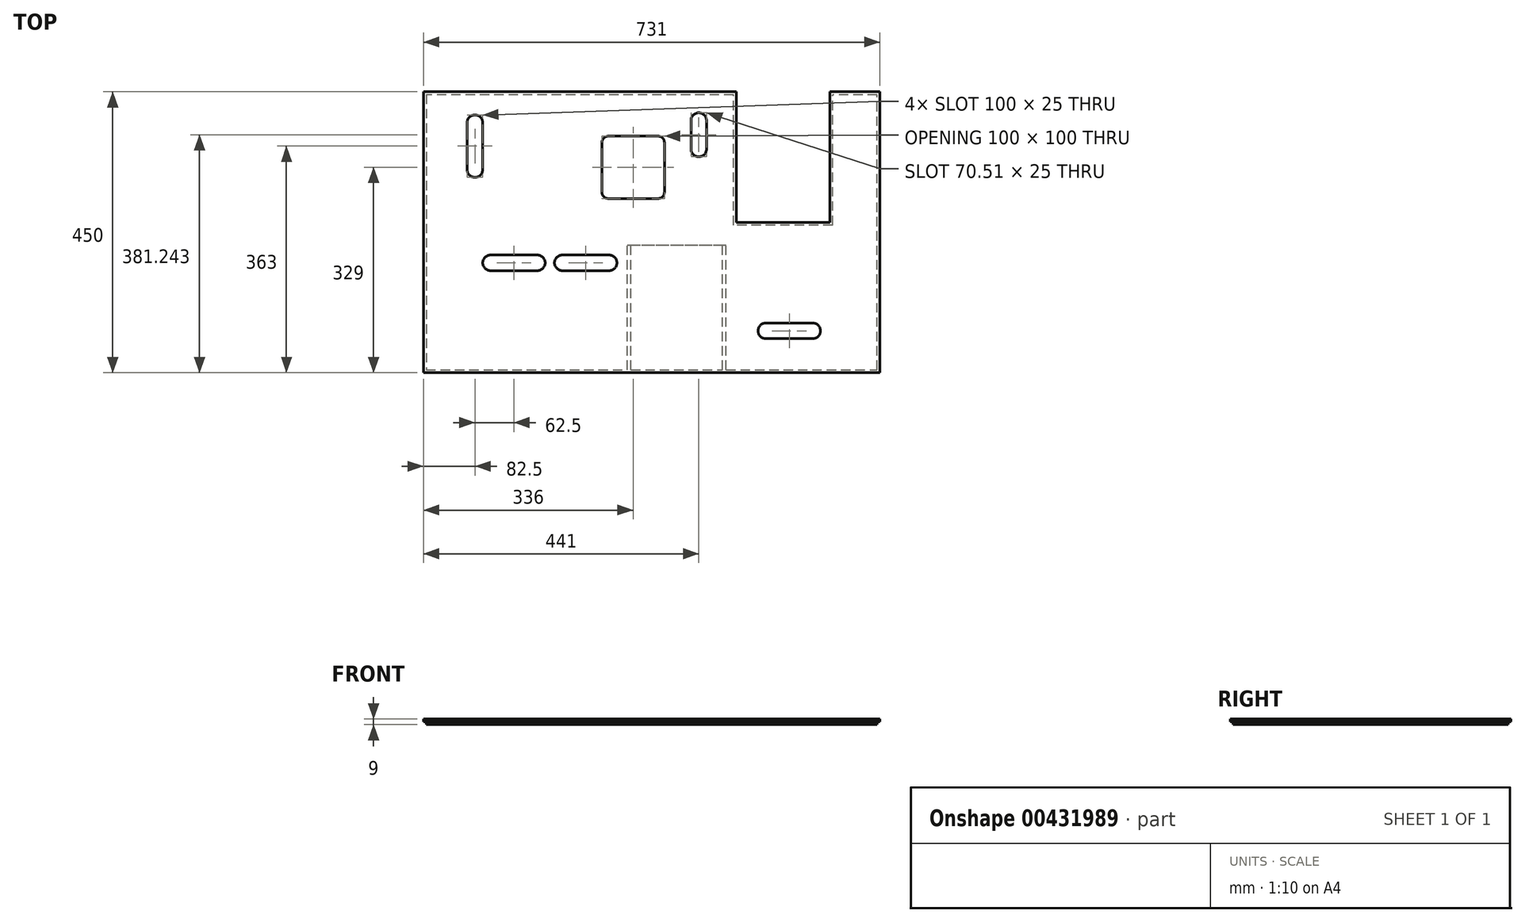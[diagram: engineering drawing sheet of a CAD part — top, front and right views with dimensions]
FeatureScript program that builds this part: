
annotation { "Feature Type Name" : "Feature", "Feature Type Description" : "" }
export const myFeature = defineFeature(function(context is Context, id is Id, definition is map)
    precondition{}
    {
        {
            var Q0;
            Q0=qCreatedBy(makeId("Top.planeOp"),FACE);
            var sketch = newSketch(context, id + "F0", { "sketchPlane" : qUnion([Q0])});
            skLineSegment(sketch, "E0.bottom", {"start": v(-365.5, 225) * mm, "end": v(365.5, 225) * mm});
            skLineSegment(sketch, "E0.top", {"start": v(-365.5, -225) * mm, "end": v(365.5, -225) * mm});
            skLineSegment(sketch, "E0.left", {"start": v(-365.5, 225) * mm, "end": v(-365.5, -225) * mm});
            skLineSegment(sketch, "E0.right", {"start": v(365.5, 225) * mm, "end": v(365.5, -225) * mm});
            skPoint(sketch, "E0.middle", {"position": v(0, 0) * mm});
            skSolve(sketch);
        }
        {
            var Q0;
            Q0=makeQuery(id+"F0.imprint","IMPRINT",FACE,{"disambiguationData":[TD([[makeQuery(id+"F0.imprint","IMPRINT",EDGE,{"derivedFrom":sQuery(id+"F0.wireOp",EDGE,"E0.bottom")}),-1.0]])]});
            extrude(context, id + "F1", {"entities" : qUnion([Q0]), "depth" : 9 * mm, "offsetDistance" : 25 * mm});
        }
        {
            var Q0;
            Q0=makeQuery(id+"F1.opExtrude","CAP_FACE",FACE,{"disambiguationData":[OSD([sQuery(id+"F0.wireOp",EDGE,"E0.bottom"),sQuery(id+"F0.wireOp",EDGE,"E0.top"),sQuery(id+"F0.wireOp",EDGE,"E0.left"),sQuery(id+"F0.wireOp",EDGE,"E0.right")])],"isStart":true});
            var sketch = newSketch(context, id + "F2", { "sketchPlane" : qUnion([Q0])});
            skLineSegment(sketch, "E1.0", {"start": v(-361, -220.5) * mm, "end": v(-361, 220.5) * mm});
            skLineSegment(sketch, "E1.1", {"start": v(361, -220.5) * mm, "end": v(-361, -220.5) * mm});
            skLineSegment(sketch, "E1.2", {"start": v(361, 220.5) * mm, "end": v(361, -220.5) * mm});
            skLineSegment(sketch, "E1.3", {"start": v(-361, 220.5) * mm, "end": v(361, 220.5) * mm});
            skLineSegment(sketch, "E2.bottom", {"start": v(-365.5, -225) * mm, "end": v(365.5, -225) * mm});
            skLineSegment(sketch, "E2.top", {"start": v(-365.5, 225) * mm, "end": v(365.5, 225) * mm});
            skLineSegment(sketch, "E2.left", {"start": v(-365.5, 225) * mm, "end": v(-365.5, -225) * mm});
            skLineSegment(sketch, "E2.right", {"start": v(365.5, 225) * mm, "end": v(365.5, -225) * mm});
            skPoint(sketch, "E2.middle", {"position": v(0, 0) * mm});
            skSolve(sketch);
        }
        {
            var Q0;
            Q0=qSketchRegion(id+"F2",true);
            extrude(context, id + "F3", {"entities" : qUnion([Q0]), "operationType" : NewBodyOperationType.REMOVE, "oppositeDirection" : true, "depth" : 4.5 * mm, "offsetDistance" : 25 * mm});
        }
        {
            var Q0;
            Q0=makeQuery(id+"F1.opExtrude","SWEPT_FACE",FACE,{"disambiguationData":[OSD([sQuery(id+"F0.wireOp",EDGE,"E0.bottom")])]});
            var sketch = newSketch(context, id + "F4", { "sketchPlane" : qUnion([Q0])});
            skLineSegment(sketch, "E3.bottom", {"start": v(-285.5, 0) * mm, "end": v(-135.5, 0) * mm});
            skLineSegment(sketch, "E3.top", {"start": v(-285.5, 9) * mm, "end": v(-135.5, 9) * mm});
            skLineSegment(sketch, "E3.left", {"start": v(-285.5, 0) * mm, "end": v(-285.5, 9) * mm});
            skLineSegment(sketch, "E3.right", {"start": v(-135.5, 0) * mm, "end": v(-135.5, 9) * mm});
            skSolve(sketch);
        }
        {
            var Q0;
            Q0=qSketchRegion(id+"F4",true);
            extrude(context, id + "F5", {"entities" : qUnion([Q0]), "operationType" : NewBodyOperationType.REMOVE, "oppositeDirection" : true, "depth" : (174 + 35) * mm, "offsetDistance" : 25 * mm});
        }
        {
            var Q0;
            Q0=makeQuery(id+"F1.opExtrude","CAP_FACE",FACE,{"disambiguationData":[OSD([sQuery(id+"F0.wireOp",EDGE,"E0.bottom"),sQuery(id+"F0.wireOp",EDGE,"E0.top"),sQuery(id+"F0.wireOp",EDGE,"E0.left"),sQuery(id+"F0.wireOp",EDGE,"E0.right")])],"isStart":true});
            var sketch = newSketch(context, id + "F6", { "sketchPlane" : qUnion([Q0])});
            skLineSegment(sketch, "E4.0", {"start": v(290, -16) * mm, "end": v(290, -225) * mm});
            skLineSegment(sketch, "E4.2", {"start": v(131, -16) * mm, "end": v(131, -225) * mm});
            skLineSegment(sketch, "E5", {"start": v(285.5, -225) * mm, "end": v(285.5, -16) * mm});
            skLineSegment(sketch, "E6", {"start": v(285.5, -16) * mm, "end": v(135.5, -16) * mm});
            skLineSegment(sketch, "E7", {"start": v(135.5, -16) * mm, "end": v(135.5, -225) * mm});
            skLineSegment(sketch, "E8", {"start": v(135.5, -225) * mm, "end": v(131, -225) * mm});
            skLineSegment(sketch, "E9", {"start": v(135.5, -16) * mm, "end": v(131, -16) * mm});
            skLineSegment(sketch, "E10", {"start": v(285.5, -16) * mm, "end": v(290, -16) * mm});
            skLineSegment(sketch, "E11", {"start": v(290, -225) * mm, "end": v(285.5, -225) * mm});
            skSolve(sketch);
        }
        {
            var Q0;
            Q0=qSketchRegion(id+"F6",true);
            extrude(context, id + "F7", {"entities" : qUnion([Q0]), "operationType" : NewBodyOperationType.REMOVE, "oppositeDirection" : true, "depth" : 4.5 * mm, "offsetDistance" : 25 * mm});
        }
        {
            var Q0;
            Q0=makeQuery(id+"F1.opExtrude","CAP_FACE",FACE,{"disambiguationData":[OSD([sQuery(id+"F0.wireOp",EDGE,"E0.bottom"),sQuery(id+"F0.wireOp",EDGE,"E0.top"),sQuery(id+"F0.wireOp",EDGE,"E0.left"),sQuery(id+"F0.wireOp",EDGE,"E0.right")])],"isStart":true});
            var sketch = newSketch(context, id + "F8", { "sketchPlane" : qUnion([Q0])});
            skLineSegment(sketch, "E12.bottom", {"start": v(290, -16) * mm, "end": v(131, -16) * mm});
            skLineSegment(sketch, "E12.top", {"start": v(290, -11.5) * mm, "end": v(131, -11.5) * mm});
            skLineSegment(sketch, "E12.left", {"start": v(290, -16) * mm, "end": v(290, -11.5) * mm});
            skLineSegment(sketch, "E12.right", {"start": v(131, -16) * mm, "end": v(131, -11.5) * mm});
            skSolve(sketch);
        }
        {
            var Q0;
            Q0 = qSketchRegion(id + "F8", true);
            extrude(context, id + "F9", {"entities" : qUnion([Q0]), "operationType" : NewBodyOperationType.REMOVE, "oppositeDirection" : true, "depth" : 4.5 * mm, "offsetDistance" : 25 * mm});
        }
        {
            var Q0;
            Q0=makeQuery(id+"F1.opExtrude","CAP_FACE",FACE,{"disambiguationData":[OSD([sQuery(id+"F0.wireOp",EDGE,"E0.bottom"),sQuery(id+"F0.wireOp",EDGE,"E0.top"),sQuery(id+"F0.wireOp",EDGE,"E0.left"),sQuery(id+"F0.wireOp",EDGE,"E0.right")])],"isStart":false});
            var sketch = newSketch(context, id + "F10", { "sketchPlane" : qUnion([Q0])});
            skArc(sketch, "E13", {"start": v(88, 179) * mm, "mid": v(75.5, 191.5) * mm, "end": v(63, 179) * mm});
            skArc(sketch, "E14", {"start": v(63, 133.49) * mm, "mid": v(75.5, 120.99) * mm, "end": v(88, 133.49) * mm});
            skLineSegment(sketch, "E15", {"start": v(75.5, 179) * mm, "end": v(63, 179) * mm, "construction": true});
            skLineSegment(sketch, "E16", {"start": v(75.5, 133.49) * mm, "end": v(88, 133.49) * mm, "construction": true});
            skLineSegment(sketch, "E17.bottom", {"start": v(63, 179) * mm, "end": v(88, 179) * mm});
            skLineSegment(sketch, "E17.top", {"start": v(63, 133.49) * mm, "end": v(88, 133.49) * mm});
            skLineSegment(sketch, "E17.left", {"start": v(63, 179) * mm, "end": v(63, 133.49) * mm});
            skLineSegment(sketch, "E17.right", {"start": v(88, 179) * mm, "end": v(88, 133.49) * mm});
            skSolve(sketch);
        }
        {
            var Q0;
            Q0=qSketchRegion(id+"F10",true);
            extrude(context, id + "F11", {"entities" : qUnion([Q0]), "operationType" : NewBodyOperationType.REMOVE, "endBound" : BoundingType.THROUGH_ALL, "oppositeDirection" : true, "depth" : 25 * mm});
        }
        {
            var Q0;
            Q0=makeQuery(id+"F1.opExtrude","CAP_FACE",FACE,{"disambiguationData":[OSD([sQuery(id+"F0.wireOp",EDGE,"E0.bottom"),sQuery(id+"F0.wireOp",EDGE,"E0.top"),sQuery(id+"F0.wireOp",EDGE,"E0.left"),sQuery(id+"F0.wireOp",EDGE,"E0.right")])],"isStart":false});
            var sketch = newSketch(context, id + "F12", { "sketchPlane" : qUnion([Q0])});
            skLineSegment(sketch, "E18.bottom", {"start": v(-258, -36.5) * mm, "end": v(-183, -36.5) * mm});
            skLineSegment(sketch, "E18.top", {"start": v(-258, -61.5) * mm, "end": v(-183, -61.5) * mm});
            skLineSegment(sketch, "E19.bottom", {"start": v(-143, -36.5) * mm, "end": v(-68, -36.5) * mm});
            skLineSegment(sketch, "E19.top", {"start": v(-143, -61.5) * mm, "end": v(-68, -61.5) * mm});
            skArc(sketch, "E20", {"start": v(-258, -36.5) * mm, "mid": v(-270.5, -49) * mm, "end": v(-258, -61.5) * mm});
            skArc(sketch, "E21", {"start": v(-183, -61.5) * mm, "mid": v(-170.5, -49) * mm, "end": v(-183, -36.5) * mm});
            skArc(sketch, "E22", {"start": v(-143, -36.5) * mm, "mid": v(-155.5, -49) * mm, "end": v(-143, -61.5) * mm});
            skArc(sketch, "E23", {"start": v(-68, -61.5) * mm, "mid": v(-55.5, -49) * mm, "end": v(-68, -36.5) * mm});
            skSolve(sketch);
        }
        {
            var Q0;
            Q0=qSketchRegion(id+"F12",true);
            extrude(context, id + "F13", {"entities" : qUnion([Q0]), "operationType" : NewBodyOperationType.REMOVE, "endBound" : BoundingType.THROUGH_ALL, "oppositeDirection" : true, "depth" : 25 * mm});
        }
        {
            var Q0;
            Q0=makeQuery(id+"F1.opExtrude","CAP_FACE",FACE,{"disambiguationData":[OSD([sQuery(id+"F0.wireOp",EDGE,"E0.bottom"),sQuery(id+"F0.wireOp",EDGE,"E0.top"),sQuery(id+"F0.wireOp",EDGE,"E0.left"),sQuery(id+"F0.wireOp",EDGE,"E0.right")])],"isStart":false});
            var sketch = newSketch(context, id + "F14", { "sketchPlane" : qUnion([Q0])});
            skLineSegment(sketch, "E24.left", {"start": v(-295.5, 175.5) * mm, "end": v(-295.5, 100.5) * mm});
            skLineSegment(sketch, "E24.right", {"start": v(-270.5, 175.5) * mm, "end": v(-270.5, 100.5) * mm});
            skArc(sketch, "E25", {"start": v(-270.5, 175.5) * mm, "mid": v(-283, 188) * mm, "end": v(-295.5, 175.5) * mm});
            skArc(sketch, "E26", {"start": v(-295.5, 100.5) * mm, "mid": v(-283, 88) * mm, "end": v(-270.5, 100.5) * mm});
            skSolve(sketch);
        }
        {
            var Q0;
            Q0=qSketchRegion(id+"F14",true);
            extrude(context, id + "F15", {"entities" : qUnion([Q0]), "operationType" : NewBodyOperationType.REMOVE, "endBound" : BoundingType.UP_TO_NEXT, "oppositeDirection" : true, "depth" : 25 * mm});
        }
        {
            var Q0;
            Q0=makeQuery(id+"F1.opExtrude","CAP_FACE",FACE,{"disambiguationData":[OSD([sQuery(id+"F0.wireOp",EDGE,"E0.bottom"),sQuery(id+"F0.wireOp",EDGE,"E0.top"),sQuery(id+"F0.wireOp",EDGE,"E0.left"),sQuery(id+"F0.wireOp",EDGE,"E0.right")])],"isStart":true});
            var sketch = newSketch(context, id + "F16", { "sketchPlane" : qUnion([Q0])});
            skLineSegment(sketch, "E27.bottom", {"start": v(-79.5, -154) * mm, "end": v(20.5, -154) * mm});
            skLineSegment(sketch, "E27.top", {"start": v(-79.5, -54) * mm, "end": v(20.5, -54) * mm});
            skLineSegment(sketch, "E27.left", {"start": v(-79.5, -154) * mm, "end": v(-79.5, -54) * mm});
            skLineSegment(sketch, "E27.right", {"start": v(20.5, -154) * mm, "end": v(20.5, -54) * mm});
            skPoint(sketch, "E27.middle", {"position": v(-29.5, -104) * mm});
            skSolve(sketch);
        }
        {
            var Q0;
            Q0=qSketchRegion(id+"F16",true);
            extrude(context, id + "F17", {"entities" : qUnion([Q0]), "operationType" : NewBodyOperationType.REMOVE, "endBound" : BoundingType.UP_TO_NEXT, "oppositeDirection" : true, "depth" : 25 * mm});
        }
        {
            var Q0;
            Q0=makeQuery(id+"F17.boolean.opBoolean","COPY",EDGE,{"derivedFrom":makeQuery(id+"F17.opExtrude","SWEPT_EDGE",EDGE,{"disambiguationData":[OSD([sQuery(id+"F16.wireOp",EDGE,"E27.bottom"),sQuery(id+"F16.wireOp",EDGE,"E27.right")])]})});
            var Q1;
            Q1=makeQuery(id+"F17.boolean.opBoolean","COPY",EDGE,{"derivedFrom":makeQuery(id+"F17.opExtrude","SWEPT_EDGE",EDGE,{"disambiguationData":[OSD([sQuery(id+"F16.wireOp",EDGE,"E27.bottom"),sQuery(id+"F16.wireOp",EDGE,"E27.left")])]})});
            var Q2;
            Q2=makeQuery(id+"F17.boolean.opBoolean","COPY",EDGE,{"derivedFrom":makeQuery(id+"F17.opExtrude","SWEPT_EDGE",EDGE,{"disambiguationData":[OSD([sQuery(id+"F16.wireOp",EDGE,"E27.top"),sQuery(id+"F16.wireOp",EDGE,"E27.left")])]})});
            var Q3;
            Q3=makeQuery(id+"F17.boolean.opBoolean","COPY",EDGE,{"derivedFrom":makeQuery(id+"F17.opExtrude","SWEPT_EDGE",EDGE,{"disambiguationData":[OSD([sQuery(id+"F16.wireOp",EDGE,"E27.top"),sQuery(id+"F16.wireOp",EDGE,"E27.right")])]})});
            fillet(context, id + "F18", {"entities" : qUnion([Q0, Q1, Q2, Q3]), "radius" : 10 * mm, "tangentPropagation" : true, "allowEdgeOverflow" : false});
        }
        {
            var Q0;
            Q0=makeQuery(id+"F1.opExtrude","CAP_FACE",FACE,{"disambiguationData":[OSD([sQuery(id+"F0.wireOp",EDGE,"E0.bottom"),sQuery(id+"F0.wireOp",EDGE,"E0.top"),sQuery(id+"F0.wireOp",EDGE,"E0.left"),sQuery(id+"F0.wireOp",EDGE,"E0.right")])],"isStart":false});
            var sketch = newSketch(context, id + "F19", { "sketchPlane" : qUnion([Q0])});
            skLineSegment(sketch, "E28.bottom", {"start": v(258, -145.5) * mm, "end": v(183, -145.5) * mm});
            skLineSegment(sketch, "E28.top", {"start": v(258, -170.5) * mm, "end": v(183, -170.5) * mm});
            skPoint(sketch, "E28.middle", {"position": v(220.5, -158) * mm});
            skArc(sketch, "E29", {"start": v(183, -145.5) * mm, "mid": v(170.5, -158) * mm, "end": v(183, -170.5) * mm});
            skArc(sketch, "E30", {"start": v(258, -170.5) * mm, "mid": v(270.5, -158) * mm, "end": v(258, -145.5) * mm});
            skSolve(sketch);
        }
        {
            var Q0;
            Q0=qSketchRegion(id+"F19",true);
            extrude(context, id + "F20", {"entities" : qUnion([Q0]), "operationType" : NewBodyOperationType.REMOVE, "endBound" : BoundingType.UP_TO_NEXT, "oppositeDirection" : true, "depth" : 25 * mm});
        }
        {
            var Q0;
            Q0=makeQuery(id+"F1.opExtrude","CAP_FACE",FACE,{"disambiguationData":[OSD([sQuery(id+"F0.wireOp",EDGE,"E0.bottom"),sQuery(id+"F0.wireOp",EDGE,"E0.top"),sQuery(id+"F0.wireOp",EDGE,"E0.left"),sQuery(id+"F0.wireOp",EDGE,"E0.right")])],"isStart":true});
            var sketch = newSketch(context, id + "F21", { "sketchPlane" : qUnion([Q0])});
            skLineSegment(sketch, "E31.bottom", {"start": v(-39, 220.5) * mm, "end": v(-33, 220.5) * mm});
            skLineSegment(sketch, "E31.top", {"start": v(-39, 20.5) * mm, "end": v(-33, 20.5) * mm});
            skLineSegment(sketch, "E31.left", {"start": v(-39, 220.5) * mm, "end": v(-39, 20.5) * mm});
            skLineSegment(sketch, "E31.right", {"start": v(-33, 220.5) * mm, "end": v(-33, 20.5) * mm});
            skLineSegment(sketch, "E32.bottom", {"start": v(113.5, 220.5) * mm, "end": v(119.5, 220.5) * mm});
            skLineSegment(sketch, "E32.top", {"start": v(113.5, 20.5) * mm, "end": v(119.5, 20.5) * mm});
            skLineSegment(sketch, "E32.left", {"start": v(113.5, 220.5) * mm, "end": v(113.5, 20.5) * mm});
            skLineSegment(sketch, "E32.right", {"start": v(119.5, 220.5) * mm, "end": v(119.5, 20.5) * mm});
            skSolve(sketch);
        }
        {
            var Q0;
            Q0 = qSketchRegion(id + "F21", true);
            extrude(context, id + "F22", {"entities" : qUnion([Q0]), "operationType" : NewBodyOperationType.REMOVE, "oppositeDirection" : true, "depth" : 4.5 * mm, "offsetDistance" : 25 * mm});
        }
        {
            var Q0;
            Q0=makeQuery(id+"F1.opExtrude","CAP_FACE",FACE,{"disambiguationData":[OSD([sQuery(id+"F0.wireOp",EDGE,"E0.bottom"),sQuery(id+"F0.wireOp",EDGE,"E0.top"),sQuery(id+"F0.wireOp",EDGE,"E0.left"),sQuery(id+"F0.wireOp",EDGE,"E0.right")])],"isStart":true});
            var sketch = newSketch(context, id + "F23", { "sketchPlane" : qUnion([Q0])});
            skLineSegment(sketch, "E33.bottom", {"start": v(-33, 220.5) * mm, "end": v(113.5, 220.5) * mm});
            skLineSegment(sketch, "E33.top", {"start": v(-33, 20.5) * mm, "end": v(113.5, 20.5) * mm});
            skLineSegment(sketch, "E33.left", {"start": v(-33, 220.5) * mm, "end": v(-33, 20.5) * mm});
            skLineSegment(sketch, "E33.right", {"start": v(113.5, 220.5) * mm, "end": v(113.5, 20.5) * mm});
            skSolve(sketch);
        }
        {
            var Q0;
            Q0 = qSketchRegion(id + "F23", true);
            extrude(context, id + "F24", {"entities" : qUnion([Q0]), "operationType" : NewBodyOperationType.REMOVE, "oppositeDirection" : true, "depth" : 2 * mm, "offsetDistance" : 25 * mm});
        }
    });
